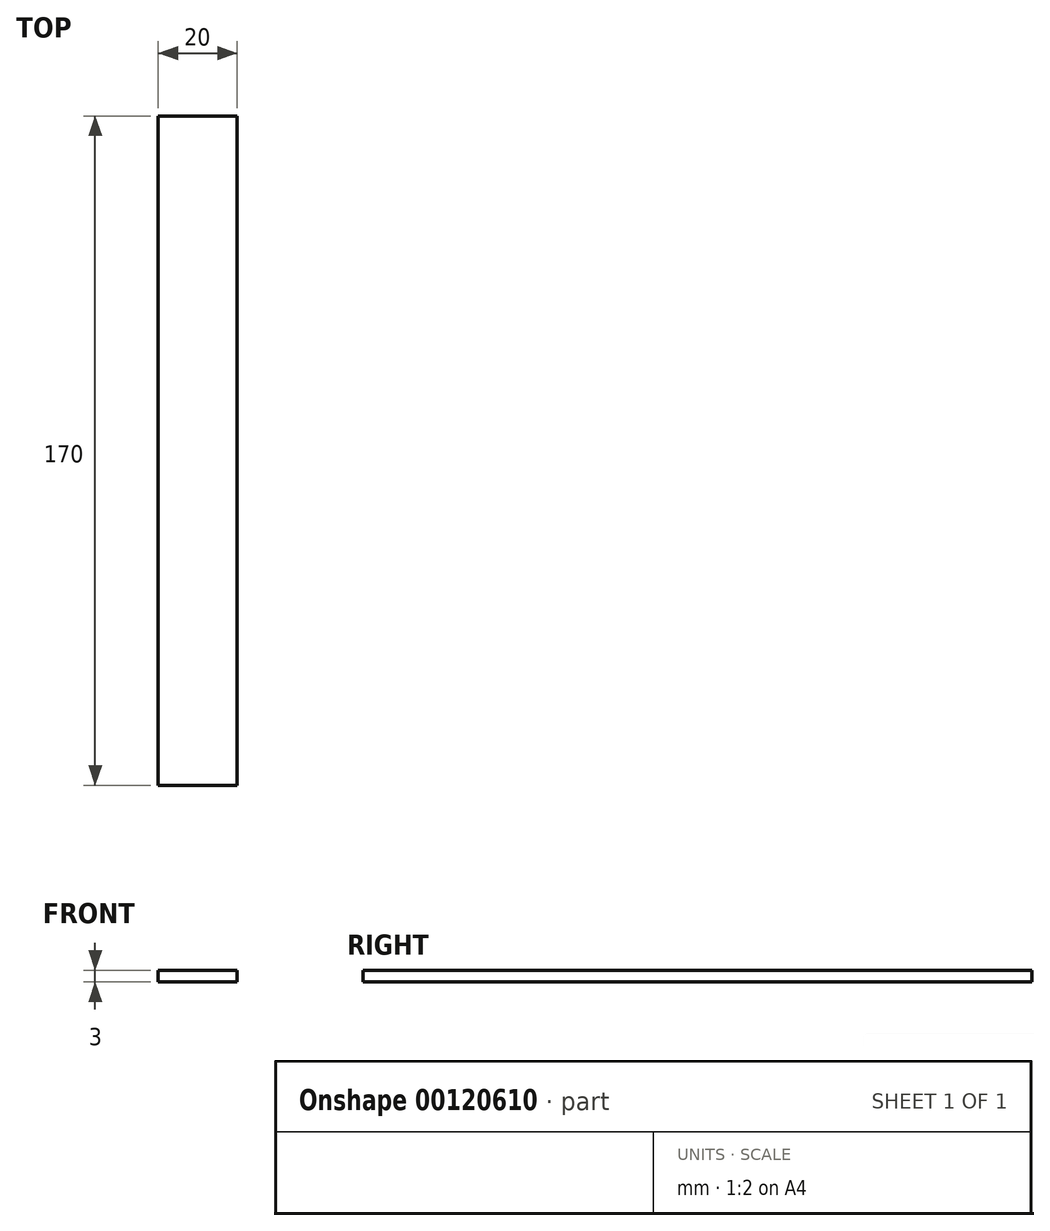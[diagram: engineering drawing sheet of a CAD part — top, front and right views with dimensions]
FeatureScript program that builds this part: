
annotation { "Feature Type Name" : "Feature", "Feature Type Description" : "" }
export const myFeature = defineFeature(function(context is Context, id is Id, definition is map)
    precondition{}
    {
        {
            var Q0;
            Q0=qCreatedBy(makeId("Top.planeOp"),FACE);
            var sketch = newSketch(context, id + "F0", { "sketchPlane" : qUnion([Q0])});
            skLineSegment(sketch, "E0.bottom", {"start": v(-44.42, 109.32) * mm, "end": v(-24.42, 109.32) * mm});
            skLineSegment(sketch, "E0.top", {"start": v(-44.42, -60.68) * mm, "end": v(-24.42, -60.68) * mm});
            skLineSegment(sketch, "E0.left", {"start": v(-44.42, 109.32) * mm, "end": v(-44.42, -60.68) * mm});
            skLineSegment(sketch, "E0.right", {"start": v(-24.42, 109.32) * mm, "end": v(-24.42, -60.68) * mm});
            skSolve(sketch);
        }
        {
            var Q0;
            Q0=makeQuery(id+"F0.imprint","IMPRINT",FACE,{"disambiguationData":[TD([[makeQuery(id+"F0.imprint","IMPRINT",EDGE,{"derivedFrom":sQuery(id+"F0.wireOp",EDGE,"E0.bottom")}),-1.0]])]});
            extrude(context, id + "F1", {"entities" : qUnion([Q0]), "depth" : 3 * mm});
        }
    });
